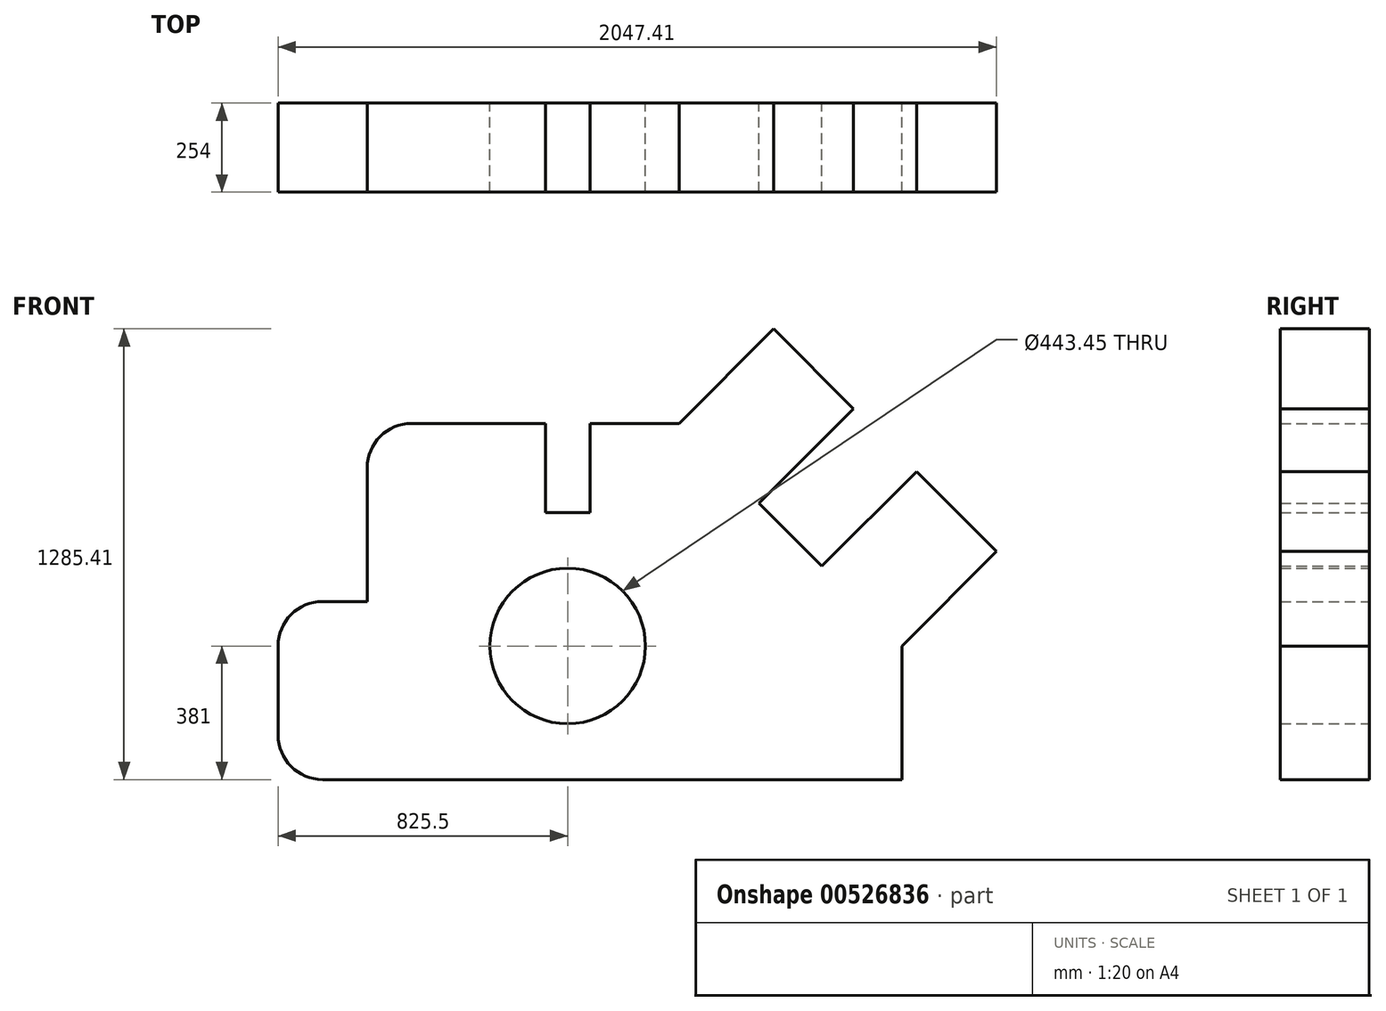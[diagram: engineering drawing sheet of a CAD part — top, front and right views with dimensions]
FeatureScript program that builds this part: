
annotation { "Feature Type Name" : "Feature", "Feature Type Description" : "" }
export const myFeature = defineFeature(function(context is Context, id is Id, definition is map)
    precondition{}
    {
        {
            var Q0;
            Q0=qCreatedBy(makeId("Front.planeOp"),FACE);
            var sketch = newSketch(context, id + "F0", { "sketchPlane" : qUnion([Q0])});
            skLineSegment(sketch, "E0", {"start": v(127, 0) * mm, "end": v(1778, 0) * mm});
            skLineSegment(sketch, "E1", {"start": v(1778, 0) * mm, "end": v(1778, 381) * mm});
            skLineSegment(sketch, "E2", {"start": v(0, 127) * mm, "end": v(0, 381) * mm});
            skPoint(sketch, "E3.visualSharp", {"position": v(0, 0) * mm});
            skArc(sketch, "E3.filletArc", {"start": v(0, 127) * mm, "mid": v(37.2, 37.2) * mm, "end": v(127, 0) * mm});
            skCircle(sketch, "E4", {"center": v(825.5, 381) * mm, "radius": 221.73 * mm});
            skLineSegment(sketch, "E5", {"start": v(127, 508) * mm, "end": v(254, 508) * mm});
            skLineSegment(sketch, "E6", {"start": v(254, 508) * mm, "end": v(254, 889) * mm});
            skLineSegment(sketch, "E7", {"start": v(381, 1016) * mm, "end": v(762, 1016) * mm});
            skLineSegment(sketch, "E8", {"start": v(762, 1016) * mm, "end": v(762, 762) * mm});
            skLineSegment(sketch, "E9", {"start": v(762, 762) * mm, "end": v(889, 762) * mm});
            skLineSegment(sketch, "E10", {"start": v(889, 762) * mm, "end": v(889, 1016) * mm});
            skLineSegment(sketch, "E11", {"start": v(889, 1016) * mm, "end": v(1143, 1016) * mm});
            skLineSegment(sketch, "E12", {"start": v(1778, 381) * mm, "end": v(2047.4, 650.4) * mm});
            skLineSegment(sketch, "E13", {"start": v(2047.4, 650.4) * mm, "end": v(1819.71, 878.1) * mm});
            skLineSegment(sketch, "E14", {"start": v(1819.71, 878.1) * mm, "end": v(1550.3, 608.7) * mm});
            skLineSegment(sketch, "E15", {"start": v(1550.3, 608.7) * mm, "end": v(1370.7, 788.3) * mm});
            skLineSegment(sketch, "E16", {"start": v(1370.7, 788.3) * mm, "end": v(1640.1, 1057.71) * mm});
            skLineSegment(sketch, "E17", {"start": v(1640.1, 1057.71) * mm, "end": v(1412.4, 1285.4) * mm});
            skLineSegment(sketch, "E18", {"start": v(1412.4, 1285.4) * mm, "end": v(1143, 1016) * mm});
            skPoint(sketch, "E19.visualSharp", {"position": v(0, 508) * mm});
            skArc(sketch, "E19.filletArc", {"start": v(127, 508) * mm, "mid": v(37.2, 470.8) * mm, "end": v(0, 381) * mm});
            skPoint(sketch, "E20.visualSharp", {"position": v(254, 1016) * mm});
            skArc(sketch, "E20.filletArc", {"start": v(381, 1016) * mm, "mid": v(291.2, 978.8) * mm, "end": v(254, 889) * mm});
            skSolve(sketch);
        }
        {
            var Q0;
            Q0=makeQuery(id+"F0.imprint","IMPRINT",FACE,{"disambiguationData":[TD([[makeQuery(id+"F0.imprint","IMPRINT",EDGE,{"derivedFrom":sQuery(id+"F0.wireOp",EDGE,"E0")}),1.0]])]});
            extrude(context, id + "F1", {"entities" : qUnion([Q0]), "depth" : 254 * mm, "offsetDistance" : 25.4 * mm});
        }
    });
